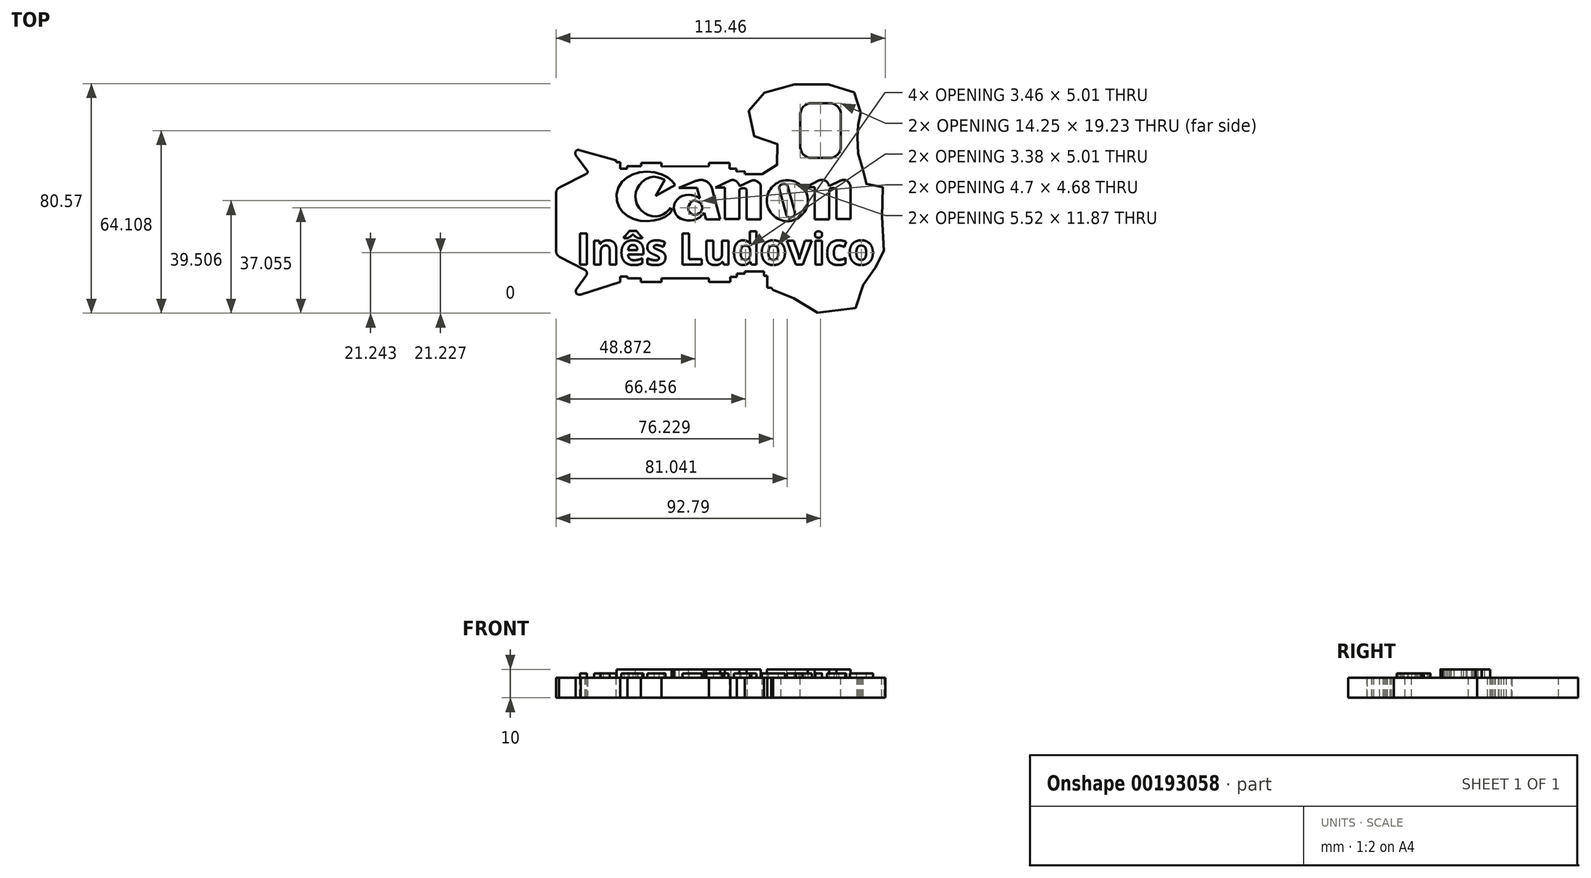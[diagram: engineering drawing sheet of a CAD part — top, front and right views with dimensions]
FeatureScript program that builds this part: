
annotation { "Feature Type Name" : "Feature", "Feature Type Description" : "" }
export const myFeature = defineFeature(function(context is Context, id is Id, definition is map)
    precondition{}
    {
        {
            var Q0;
            Q0=qCreatedBy(makeId("Top.planeOp"),FACE);
            var sketch = newSketch(context, id + "F0", { "sketchPlane" : qUnion([Q0])});
            skLineSegment(sketch, "E0", {"start": v(25.55, 22.7) * mm, "end": v(22.34, 17.11) * mm});
            skLineSegment(sketch, "E1", {"start": v(22.34, 17.11) * mm, "end": v(29.25, 20.87) * mm});
            skLineSegment(sketch, "E2", {"start": v(27.55, 12.91) * mm, "end": v(28.1, 11.89) * mm});
            skLineSegment(sketch, "E3", {"start": v(36.86, 19.9) * mm, "end": v(30.53, 19.9) * mm});
            skLineSegment(sketch, "E4", {"start": v(30.53, 19.9) * mm, "end": v(36.65, 22.37) * mm});
            skLineSegment(sketch, "E5", {"start": v(36.86, 19.9) * mm, "end": v(37.86, 16.15) * mm});
            skLineSegment(sketch, "E6", {"start": v(39.39, 11.08) * mm, "end": v(39.97, 8.89) * mm});
            skLineSegment(sketch, "E7", {"start": v(39.97, 8.89) * mm, "end": v(44.97, 8.89) * mm});
            skLineSegment(sketch, "E8", {"start": v(44.97, 8.89) * mm, "end": v(42.04, 19.9) * mm});
            skLineSegment(sketch, "E9", {"start": v(48.66, 22.57) * mm, "end": v(43.34, 20.06) * mm});
            skLineSegment(sketch, "E10", {"start": v(43.34, 20.06) * mm, "end": v(46.62, 20.06) * mm});
            skLineSegment(sketch, "E11", {"start": v(46.62, 20.06) * mm, "end": v(46.62, 8.93) * mm});
            skLineSegment(sketch, "E12", {"start": v(46.62, 8.93) * mm, "end": v(51.76, 8.93) * mm});
            skLineSegment(sketch, "E13", {"start": v(51.76, 8.93) * mm, "end": v(51.76, 19.12) * mm});
            skLineSegment(sketch, "E14", {"start": v(54.28, 19.05) * mm, "end": v(54.28, 8.84) * mm});
            skLineSegment(sketch, "E15", {"start": v(54.28, 8.84) * mm, "end": v(59.22, 8.84) * mm});
            skLineSegment(sketch, "E16", {"start": v(59.22, 8.84) * mm, "end": v(59.22, 20.47) * mm});
            skLineSegment(sketch, "E17", {"start": v(51.83, 20.55) * mm, "end": v(55.42, 22.2) * mm});
            skCircle(sketch, "E18", {"center": v(68.54, 15.4) * mm, "radius": 7.18 * mm});
            skLineSegment(sketch, "E19", {"start": v(65.68, 19.69) * mm, "end": v(68.18, 10.33) * mm});
            skLineSegment(sketch, "E20", {"start": v(68.64, 20.6) * mm, "end": v(71.14, 11.46) * mm});
            skLineSegment(sketch, "E21", {"start": v(79.7, 22.51) * mm, "end": v(75.06, 20.1) * mm});
            skLineSegment(sketch, "E22", {"start": v(75.06, 20.1) * mm, "end": v(78.1, 20.1) * mm});
            skLineSegment(sketch, "E23", {"start": v(78.1, 20.1) * mm, "end": v(78.1, 8.88) * mm});
            skLineSegment(sketch, "E24", {"start": v(78.1, 8.88) * mm, "end": v(83.2, 8.88) * mm});
            skLineSegment(sketch, "E25", {"start": v(83.2, 8.88) * mm, "end": v(83.2, 19.16) * mm});
            skLineSegment(sketch, "E26", {"start": v(85.75, 19) * mm, "end": v(85.75, 8.9) * mm});
            skLineSegment(sketch, "E27", {"start": v(85.75, 8.9) * mm, "end": v(90.69, 8.9) * mm});
            skLineSegment(sketch, "E28", {"start": v(90.69, 8.9) * mm, "end": v(90.69, 20.51) * mm});
            skLineSegment(sketch, "E29", {"start": v(83.21, 20.55) * mm, "end": v(87.16, 22.36) * mm});
            skFitSpline(sketch, "E30", {"points": [v(87.16, 22.36) * mm, v(88.44, 22.69) * mm, v(89.84, 22.08) * mm, v(90.69, 20.51) * mm], "startDerivative": vector(4.02, 1.64) * mm, "endDerivative": vector(1.85, -4.85) * mm});
            skFitSpline(sketch, "E31", {"points": [v(79.7, 22.51) * mm, v(80.8, 22.69) * mm, v(82.34, 22.06) * mm, v(83.21, 20.55) * mm], "startDerivative": vector(3.56, 1.05) * mm, "endDerivative": vector(1.86, -4.65) * mm});
            skFitSpline(sketch, "E32", {"points": [v(83.2, 19.16) * mm, v(84, 19.77) * mm, v(85.05, 19.78) * mm, v(85.75, 19) * mm], "startDerivative": vector(1.8, 4.83) * mm, "endDerivative": vector(0.96, -4.57) * mm});
            skFitSpline(sketch, "E33", {"points": [v(65.68, 19.69) * mm, v(66, 20.79) * mm, v(67.73, 21.3) * mm, v(68.64, 20.6) * mm], "startDerivative": vector(0.1, 3.88) * mm, "endDerivative": vector(2.36, -3) * mm});
            skFitSpline(sketch, "E34", {"points": [v(71.14, 11.46) * mm, v(70.7, 9.89) * mm, v(69.36, 9.46) * mm, v(68.18, 10.33) * mm], "startDerivative": vector(1.8, -7.45) * mm, "endDerivative": vector(-2.16, 5.47) * mm});
            skFitSpline(sketch, "E35", {"points": [v(55.42, 22.2) * mm, v(56.74, 22.57) * mm, v(58.26, 21.97) * mm, v(59.22, 20.47) * mm], "startDerivative": vector(4.12, 1.85) * mm, "endDerivative": vector(0.6, -6.79) * mm});
            skFitSpline(sketch, "E36", {"points": [v(51.76, 19.12) * mm, v(52.53, 19.72) * mm, v(53.4, 19.74) * mm, v(54.28, 19.05) * mm], "startDerivative": vector(0.57, 3.43) * mm, "endDerivative": vector(1.8, -4.71) * mm});
            skFitSpline(sketch, "E37", {"points": [v(48.66, 22.57) * mm, v(49.98, 22.57) * mm, v(51.2, 21.7) * mm, v(51.83, 20.55) * mm], "startDerivative": vector(4.07, 0.59) * mm, "endDerivative": vector(1.6, -3.62) * mm});
            skFitSpline(sketch, "E38", {"points": [v(36.65, 22.37) * mm, v(38.17, 22.68) * mm, v(39.66, 22.37) * mm, v(41.07, 21.46) * mm, v(42.04, 19.9) * mm], "startDerivative": vector(6.26, 1.9) * mm, "endDerivative": vector(3.2, -6.44) * mm});
            skFitSpline(sketch, "E39", {"points": [v(37.86, 16.15) * mm, v(35.45, 17.27) * mm, v(32.42, 17.24) * mm, v(29.68, 15.5) * mm, v(28.77, 12.57) * mm, v(30.3, 9.6) * mm, v(33.67, 8.48) * mm, v(36.81, 8.95) * mm, v(39.39, 11.08) * mm], "startDerivative": vector(-20.05, 11.67) * mm, "endDerivative": vector(18.93, 19.47) * mm});
            skFitSpline(sketch, "E40", {"points": [v(35.36, 15.28) * mm, v(34.05, 13.9) * mm, v(33.97, 11.85) * mm, v(35.58, 10.54) * mm, v(37.73, 11.06) * mm, v(38.7, 12.83) * mm, v(38.02, 14.6) * mm, v(36.69, 15.3) * mm, v(35.36, 15.28) * mm]});
            skFitSpline(sketch, "E41", {"points": [v(25.55, 22.7) * mm, v(22.92, 23.67) * mm, v(19.35, 23.24) * mm, v(16.4, 20.56) * mm, v(15.28, 17.49) * mm, v(15.73, 14.19) * mm, v(17.82, 11.56) * mm, v(20.57, 10.14) * mm, v(23.96, 10.1) * mm, v(26.14, 11.31) * mm, v(27.55, 12.91) * mm], "startDerivative": vector(-26.12, 12.48) * mm, "endDerivative": vector(15.76, 20.13) * mm});
            skFitSpline(sketch, "E42", {"points": [v(29.25, 20.87) * mm, v(27.38, 22.95) * mm, v(23.88, 24.86) * mm, v(18.1, 25.5) * mm, v(13.3, 24.13) * mm, v(10.2, 21.61) * mm, v(8.67, 17.42) * mm, v(9.54, 13.21) * mm, v(12.16, 10.3) * mm, v(16.04, 8.58) * mm, v(20.51, 8.24) * mm, v(24.56, 9.21) * mm, v(26.81, 10.52) * mm, v(28.1, 11.89) * mm], "startDerivative": vector(-25.89, 32.96) * mm, "endDerivative": vector(22.29, 26.43) * mm});
            skSolve(sketch);
        }
        {
            var Q0;
            Q0=makeQuery(id+"F0.imprint","IMPRINT",FACE,{"disambiguationData":[TD([[makeQuery(id+"F0.imprint","IMPRINT",EDGE,{"derivedFrom":sQuery(id+"F0.wireOp",EDGE,"E21")}),1.0]])]});
            var Q1;
            Q1=makeQuery(id+"F0.imprint","IMPRINT",FACE,{"disambiguationData":[TD([[makeQuery(id+"F0.imprint","IMPRINT",EDGE,{"derivedFrom":sQuery(id+"F0.wireOp",EDGE,"E18")}),1.0]])]});
            var Q2;
            Q2=makeQuery(id+"F0.imprint","IMPRINT",FACE,{"disambiguationData":[TD([[makeQuery(id+"F0.imprint","IMPRINT",EDGE,{"derivedFrom":sQuery(id+"F0.wireOp",EDGE,"E9")}),1.0]])]});
            var Q3;
            Q3=makeQuery(id+"F0.imprint","IMPRINT",FACE,{"disambiguationData":[TD([[makeQuery(id+"F0.imprint","IMPRINT",EDGE,{"derivedFrom":sQuery(id+"F0.wireOp",EDGE,"E3")}),-1.0]])]});
            var Q4;
            Q4=makeQuery(id+"F0.imprint","IMPRINT",FACE,{"disambiguationData":[TD([[makeQuery(id+"F0.imprint","IMPRINT",EDGE,{"derivedFrom":sQuery(id+"F0.wireOp",EDGE,"E0")}),1.0]])]});
            extrude(context, id + "F1", {"entities" : qUnion([Q0, Q1, Q2, Q3, Q4]), "depth" : 3 * mm});
        }
        {
            var Q0;
            Q0=qCreatedBy(makeId("Top.planeOp"),FACE);
            var sketch = newSketch(context, id + "F2", { "sketchPlane" : qUnion([Q0])});
            skText(sketch, "E43", { "text": "Inês Ludovico", "fontName": "OpenSans-Bold.ttf"});
            const initialGuessF2  = {"E43": [-0.0055, -0.00706, 1, 0, 0.01106]};
            skSetInitialGuess(sketch, initialGuessF2);
            skSolve(sketch);
        }
        {
            var Q0;
            Q0 = qSketchRegion(id + "F2", true);
            extrude(context, id + "F3", {"entities" : qUnion([Q0]), "depth" : 1.5 * mm});
        }
        {
            var Q0;
            Q0=qCreatedBy(makeId("Top.planeOp"),FACE);
            var sketch = newSketch(context, id + "F4", { "sketchPlane" : qUnion([Q0])});
            skLineSegment(sketch, "E44", {"start": v(-4.27, 33.12) * mm, "end": v(8.5, 29.54) * mm});
            skLineSegment(sketch, "E45", {"start": v(8.5, 29.54) * mm, "end": v(8.5, 28.85) * mm});
            skLineSegment(sketch, "E46", {"start": v(8.5, 28.85) * mm, "end": v(9.98, 28.85) * mm});
            skLineSegment(sketch, "E47", {"start": v(9.98, 28.85) * mm, "end": v(9.98, 26.64) * mm});
            skLineSegment(sketch, "E48", {"start": v(9.98, 26.64) * mm, "end": v(12.34, 26.64) * mm});
            skLineSegment(sketch, "E49", {"start": v(12.34, 26.64) * mm, "end": v(12.34, 27.52) * mm});
            skLineSegment(sketch, "E50", {"start": v(12.34, 27.52) * mm, "end": v(17.25, 27.52) * mm});
            skLineSegment(sketch, "E51", {"start": v(17.25, 27.52) * mm, "end": v(17.25, 28.65) * mm});
            skLineSegment(sketch, "E52", {"start": v(17.25, 28.65) * mm, "end": v(24.43, 28.65) * mm});
            skLineSegment(sketch, "E53", {"start": v(24.43, 28.65) * mm, "end": v(24.43, 27.32) * mm});
            skLineSegment(sketch, "E54", {"start": v(24.43, 27.32) * mm, "end": v(41.08, 27.52) * mm});
            skPoint(sketch, "E54.endSnap0", {"position": v(14.8, 27.52) * mm});
            skLineSegment(sketch, "E55", {"start": v(41.08, 27.52) * mm, "end": v(41.07, 28.58) * mm});
            skLineSegment(sketch, "E56", {"start": v(41.07, 28.58) * mm, "end": v(48.22, 28.66) * mm});
            skLineSegment(sketch, "E57", {"start": v(48.22, 28.66) * mm, "end": v(48.25, 26.59) * mm});
            skLineSegment(sketch, "E58", {"start": v(48.25, 26.59) * mm, "end": v(50.73, 26.62) * mm});
            skLineSegment(sketch, "E59", {"start": v(50.73, 26.62) * mm, "end": v(50.74, 25.63) * mm});
            skLineSegment(sketch, "E60", {"start": v(50.74, 25.63) * mm, "end": v(53.6, 25.67) * mm});
            skLineSegment(sketch, "E61", {"start": v(53.6, 25.67) * mm, "end": v(53.6, 24.68) * mm});
            skLineSegment(sketch, "E62", {"start": v(53.6, 24.68) * mm, "end": v(59.69, 24.75) * mm});
            skFitSpline(sketch, "E63", {"points": [v(59.69, 24.75) * mm, v(60.26, 25.63) * mm, v(61.5, 26.44) * mm, v(62.74, 26.5) * mm, v(64.36, 27.37) * mm, v(65.59, 29) * mm, v(66.18, 31.16) * mm, v(66.23, 33.61) * mm, v(64.95, 35.33) * mm, v(62.98, 35.97) * mm, v(60.03, 36.37) * mm, v(57.33, 37.74) * mm, v(55.6, 39.48) * mm, v(54.53, 42.7) * mm, v(54.86, 46.33) * mm, v(55.75, 48.71) * mm, v(57.24, 50.7) * mm, v(59.17, 52.42) * mm, v(62.3, 54.24) * mm, v(66.1, 55.5) * mm, v(70.88, 56.17) * mm, v(76.66, 56.43) * mm, v(81.08, 56.38) * mm, v(85.82, 55.8) * mm, v(88.74, 55.18) * mm, v(91.03, 54.2) * mm, v(93.06, 51.8) * mm, v(93.84, 48.78) * mm, v(94, 47.13) * mm, v(94.05, 46.53) * mm, v(94.4, 46) * mm, v(94.47, 45.25) * mm, v(94.34, 44.1) * mm, v(93.9, 43.61) * mm, v(93.6, 43.28) * mm, v(93.5, 42.65) * mm, v(93.38, 41.84) * mm, v(93.53, 41.35) * mm, v(93.98, 40.92) * mm, v(94.23, 39.46) * mm, v(93.8, 38.5) * mm, v(93.3, 37.98) * mm, v(93.02, 37.4) * mm, v(93.06, 35.8) * mm, v(93.1, 33.97) * mm, v(93.1, 32.7) * mm, v(93.1, 32.15) * mm, v(93.42, 31.82) * mm, v(93.75, 31.22) * mm, v(93.84, 30.06) * mm, v(94.53, 29.32) * mm, v(95.04, 27.79) * mm, v(95, 25.6) * mm, v(94.77, 24.75) * mm, v(94.81, 23.92) * mm, v(95.6, 23) * mm, v(96.13, 22.21) * mm, v(96.35, 21.07) * mm, v(96.91, 21.07) * mm, v(98.27, 21.07) * mm, v(99.67, 21.07) * mm, v(101.12, 20.77) * mm, v(102.43, 19.28) * mm, v(102.22, 15.3) * mm, v(101.8, 10.84) * mm, v(101.68, 5.8) * mm, v(102, 0) * mm, v(102.58, -3.28) * mm, v(102.84, -5.38) * mm, v(101.88, -7.4) * mm, v(99.78, -8.18) * mm, v(97.24, -8.27) * mm, v(96.2, -10.19) * mm, v(95.5, -12.83) * mm, v(94.8, -15.64) * mm, v(94.46, -18.3) * mm, v(94, -20.63) * mm, v(91.03, -23.04) * mm, v(83.93, -24.1) * mm, v(77.9, -23.72) * mm, v(73.63, -22.18) * mm, v(71.42, -19.97) * mm, v(70.31, -18.2) * mm, v(68.55, -16.58) * mm, v(65.38, -15.92) * mm, v(63.47, -15.92) * mm], "startDerivative": vector(54.76, 104.15) * mm, "endDerivative": vector(-153.88, -5.36) * mm});
            skLineSegment(sketch, "E64", {"start": v(63.47, -15.92) * mm, "end": v(62.9, -15.16) * mm});
            skLineSegment(sketch, "E65", {"start": v(62.9, -15.16) * mm, "end": v(61.49, -15.16) * mm});
            skLineSegment(sketch, "E66", {"start": v(61.49, -15.16) * mm, "end": v(61.49, -11) * mm});
            skLineSegment(sketch, "E67", {"start": v(61.49, -11) * mm, "end": v(60.4, -11) * mm});
            skLineSegment(sketch, "E68", {"start": v(60.4, -11) * mm, "end": v(60.4, -9.49) * mm});
            skLineSegment(sketch, "E69", {"start": v(60.4, -9.49) * mm, "end": v(53.68, -9.49) * mm});
            skLineSegment(sketch, "E70", {"start": v(53.68, -9.49) * mm, "end": v(53.68, -10.27) * mm});
            skLineSegment(sketch, "E71", {"start": v(53.68, -10.27) * mm, "end": v(50.81, -10.27) * mm});
            skLineSegment(sketch, "E72", {"start": v(50.81, -10.27) * mm, "end": v(50.81, -11.3) * mm});
            skLineSegment(sketch, "E73", {"start": v(50.81, -11.3) * mm, "end": v(48.58, -11.3) * mm});
            skLineSegment(sketch, "E74", {"start": v(48.58, -11.3) * mm, "end": v(48.58, -13.08) * mm});
            skLineSegment(sketch, "E75", {"start": v(48.58, -13.08) * mm, "end": v(41.03, -13.08) * mm});
            skLineSegment(sketch, "E76", {"start": v(41.03, -13.08) * mm, "end": v(41.03, -11.83) * mm});
            skLineSegment(sketch, "E77", {"start": v(41.03, -11.83) * mm, "end": v(24.46, -11.83) * mm});
            skLineSegment(sketch, "E78", {"start": v(24.46, -11.83) * mm, "end": v(24.46, -13.08) * mm});
            skLineSegment(sketch, "E79", {"start": v(24.46, -13.08) * mm, "end": v(17.18, -13.08) * mm});
            skLineSegment(sketch, "E80", {"start": v(17.18, -13.08) * mm, "end": v(17.18, -11.83) * mm});
            skLineSegment(sketch, "E81", {"start": v(17.18, -11.83) * mm, "end": v(12.49, -11.83) * mm});
            skLineSegment(sketch, "E82", {"start": v(12.49, -11.83) * mm, "end": v(12.49, -11.25) * mm});
            skLineSegment(sketch, "E83", {"start": v(12.49, -11.25) * mm, "end": v(9.98, -11.25) * mm});
            skLineSegment(sketch, "E84", {"start": v(9.98, -11.25) * mm, "end": v(9.98, -13.08) * mm});
            skLineSegment(sketch, "E85", {"start": v(9.98, -13.08) * mm, "end": v(-3.92, -17.55) * mm});
            skLineSegment(sketch, "E86", {"start": v(-5.45, -15.73) * mm, "end": v(-1.92, -10.72) * mm});
            skLineSegment(sketch, "E87", {"start": v(-2.35, -8.98) * mm, "end": v(-11.49, -4.22) * mm});
            skLineSegment(sketch, "E88", {"start": v(-12.6, 17.98) * mm, "end": v(-12.6, -1.95) * mm});
            skLineSegment(sketch, "E89", {"start": v(-11.1, 20.15) * mm, "end": v(-2.07, 24.7) * mm});
            skLineSegment(sketch, "E90", {"start": v(-1.76, 26.16) * mm, "end": v(-5.65, 31.3) * mm});
            skFitSpline(sketch, "E91", {"points": [v(-4.27, 33.12) * mm, v(-5.17, 33.12) * mm, v(-5.86, 32.2) * mm, v(-5.65, 31.3) * mm], "startDerivative": vector(-2.87, 0.62) * mm, "endDerivative": vector(1.24, -2.69) * mm});
            skFitSpline(sketch, "E92", {"points": [v(-1.76, 26.16) * mm, v(-1.48, 25.5) * mm, v(-1.76, 24.95) * mm, v(-2.07, 24.7) * mm], "startDerivative": vector(1.15, -1.76) * mm, "endDerivative": vector(-1.11, -0.71) * mm});
            skFitSpline(sketch, "E93", {"points": [v(-11.1, 20.15) * mm, v(-11.86, 19.67) * mm, v(-12.42, 18.78) * mm, v(-12.6, 17.98) * mm], "startDerivative": vector(-2.4, -1.2) * mm, "endDerivative": vector(-0.4, -2.47) * mm});
            skFitSpline(sketch, "E94", {"points": [v(-11.49, -4.22) * mm, v(-12.1, -3.64) * mm, v(-12.48, -2.9) * mm, v(-12.6, -1.95) * mm], "startDerivative": vector(-2.05, 1.65) * mm, "endDerivative": vector(-0.19, 2.8) * mm});
            skFitSpline(sketch, "E95", {"points": [v(-2.35, -8.98) * mm, v(-1.93, -9.4) * mm, v(-1.76, -10.15) * mm, v(-1.92, -10.72) * mm], "startDerivative": vector(1.44, -1.13) * mm, "endDerivative": vector(-0.68, -1.68) * mm});
            skFitSpline(sketch, "E96", {"points": [v(-5.45, -15.73) * mm, v(-5.65, -16.45) * mm, v(-5.12, -17.41) * mm, v(-3.92, -17.55) * mm], "startDerivative": vector(-1.13, -2.3) * mm, "endDerivative": vector(3.62, 0.3) * mm});
            skLineSegment(sketch, "E97.bottom", {"start": v(77.07, 49.61) * mm, "end": v(83.32, 49.61) * mm});
            skLineSegment(sketch, "E97.top", {"start": v(77.07, 30.38) * mm, "end": v(83.32, 30.38) * mm});
            skLineSegment(sketch, "E97.left", {"start": v(73.07, 45.61) * mm, "end": v(73.07, 34.38) * mm});
            skLineSegment(sketch, "E97.right", {"start": v(87.32, 45.61) * mm, "end": v(87.32, 34.38) * mm});
            skPoint(sketch, "E98.visualSharp", {"position": v(73.07, 49.61) * mm});
            skArc(sketch, "E98.filletArc", {"start": v(77.07, 49.61) * mm, "mid": v(74.24, 48.44) * mm, "end": v(73.07, 45.61) * mm});
            skPoint(sketch, "E99.visualSharp", {"position": v(87.32, 49.61) * mm});
            skArc(sketch, "E99.filletArc", {"start": v(87.32, 45.61) * mm, "mid": v(86.14, 48.44) * mm, "end": v(83.32, 49.61) * mm});
            skPoint(sketch, "E100.visualSharp", {"position": v(73.07, 30.38) * mm});
            skArc(sketch, "E100.filletArc", {"start": v(73.07, 34.38) * mm, "mid": v(74.24, 31.55) * mm, "end": v(77.07, 30.38) * mm});
            skPoint(sketch, "E101.visualSharp", {"position": v(87.32, 30.38) * mm});
            skArc(sketch, "E101.filletArc", {"start": v(83.32, 30.38) * mm, "mid": v(86.14, 31.55) * mm, "end": v(87.32, 34.38) * mm});
            skPoint(sketch, "E102.center.orphan", {"position": v(84.14, -15.64) * mm});
            skPoint(sketch, "E103.end.orphan", {"position": v(86.67, -1.38) * mm});
            skPoint(sketch, "E104.5.internal.orphan", {"position": v(66.12, 0) * mm});
            skPoint(sketch, "E105.start.orphan", {"position": v(86.67, 17.03) * mm});
            skSolve(sketch);
        }
        {
            var Q0;
            Q0=makeQuery(id+"F4.imprint","IMPRINT",FACE,{"disambiguationData":[TD([[makeQuery(id+"F4.imprint","IMPRINT",EDGE,{"derivedFrom":sQuery(id+"F4.wireOp",EDGE,"E44")}),-1.0]])]});
            extrude(context, id + "F5", {"entities" : qUnion([Q0]), "oppositeDirection" : true, "depth" : 7 * mm});
        }
    });
